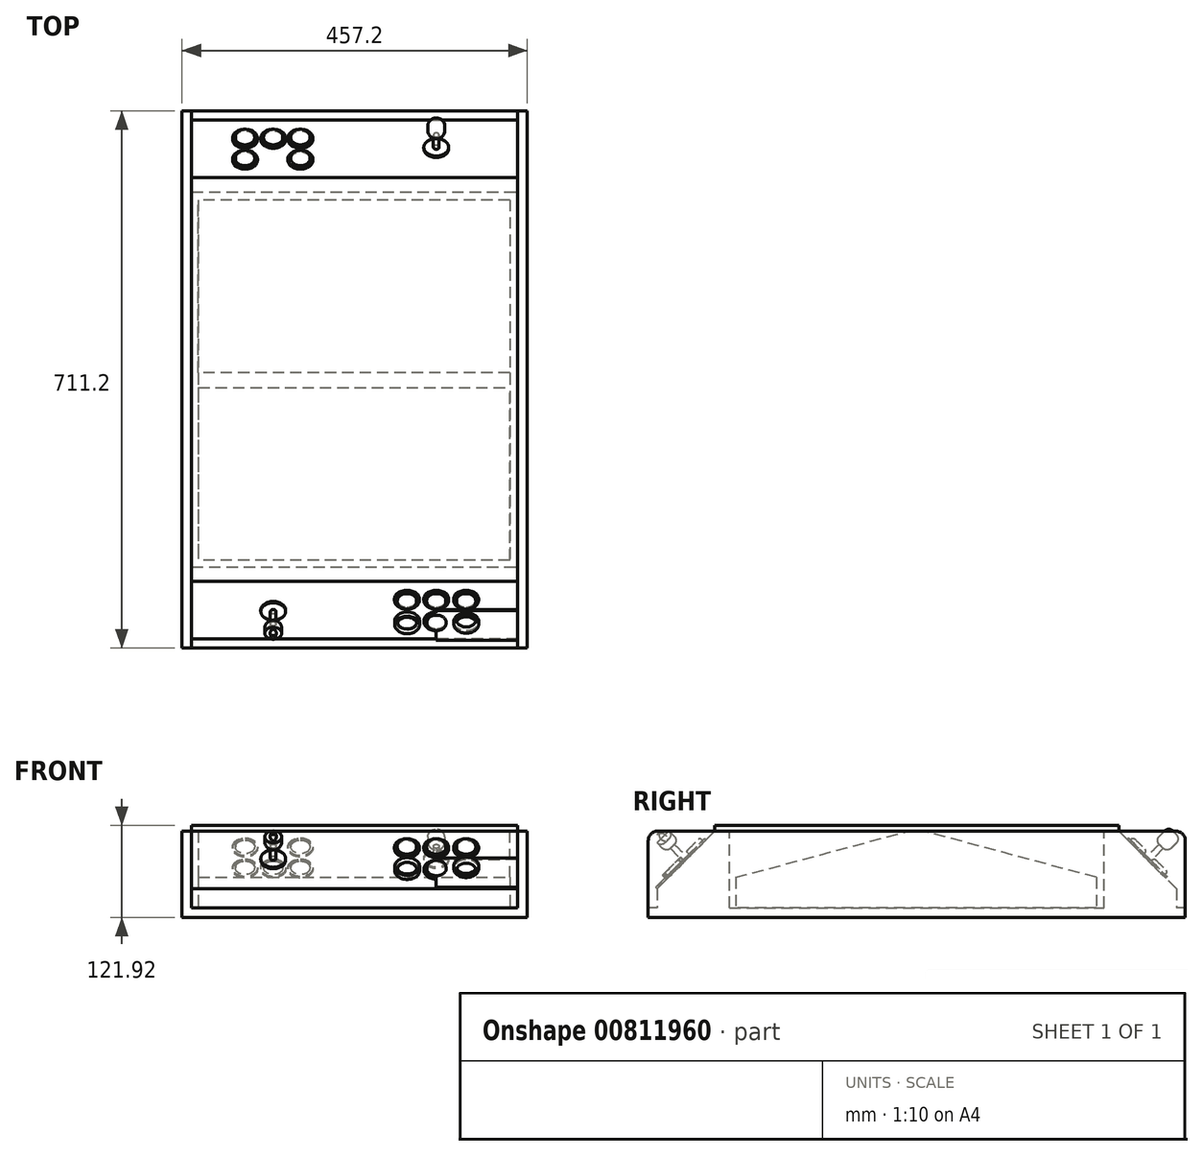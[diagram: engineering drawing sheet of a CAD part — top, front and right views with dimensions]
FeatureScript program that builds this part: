
annotation { "Feature Type Name" : "Feature", "Feature Type Description" : "" }
export const myFeature = defineFeature(function(context is Context, id is Id, definition is map)
    precondition{}
    {
        {
            var Q0;
            Q0=qCreatedBy(makeId("Top.planeOp"),FACE);
            var sketch = newSketch(context, id + "F0", { "sketchPlane" : qUnion([Q0])});
            skLineSegment(sketch, "E0.bottom", {"start": v(-402.64, 582.98) * mm, "end": v(54.56, 582.98) * mm});
            skLineSegment(sketch, "E0.top", {"start": v(-402.64, -128.22) * mm, "end": v(54.56, -128.22) * mm});
            skLineSegment(sketch, "E0.left", {"start": v(-402.64, 582.98) * mm, "end": v(-402.64, -128.22) * mm});
            skLineSegment(sketch, "E0.right", {"start": v(54.56, 582.98) * mm, "end": v(54.56, -128.22) * mm});
            skSolve(sketch);
        }
        {
            var Q0;
            Q0=qSketchRegion(id+"F0",true);
            extrude(context, id + "F1", {"entities" : qUnion([Q0]), "depth" : 12.7 * mm, "offsetDistance" : 25.4 * mm});
        }
        {
            var Q0;
            Q0=makeQuery(id+"F1.opExtrude","CAP_FACE",FACE,{"disambiguationData":[OSD([sQuery(id+"F0.wireOp",EDGE,"E0.bottom"),sQuery(id+"F0.wireOp",EDGE,"E0.top"),sQuery(id+"F0.wireOp",EDGE,"E0.left"),sQuery(id+"F0.wireOp",EDGE,"E0.right")])],"isStart":false});
            var sketch = newSketch(context, id + "F2", { "sketchPlane" : qUnion([Q0])});
            skLineSegment(sketch, "E1.left", {"start": v(54.56, 582.98) * mm, "end": v(54.56, 570.28) * mm});
            skLineSegment(sketch, "E1.right", {"start": v(-402.64, 582.98) * mm, "end": v(-402.64, 570.28) * mm});
            skLineSegment(sketch, "E2.bottom", {"start": v(-402.64, 582.98) * mm, "end": v(-389.94, 582.98) * mm});
            skLineSegment(sketch, "E2.top", {"start": v(-402.64, -128.22) * mm, "end": v(-389.94, -128.22) * mm});
            skLineSegment(sketch, "E2.left", {"start": v(-402.64, 582.98) * mm, "end": v(-402.64, -128.22) * mm});
            skLineSegment(sketch, "E2.right", {"start": v(-389.94, 582.98) * mm, "end": v(-389.94, -128.22) * mm});
            skLineSegment(sketch, "E3.left", {"start": v(54.56, -128.22) * mm, "end": v(54.56, -115.52) * mm});
            skLineSegment(sketch, "E3.right", {"start": v(-402.64, -128.22) * mm, "end": v(-402.64, -115.52) * mm});
            skLineSegment(sketch, "E4.bottom", {"start": v(54.56, 582.98) * mm, "end": v(41.86, 582.98) * mm});
            skLineSegment(sketch, "E4.top", {"start": v(54.56, -128.22) * mm, "end": v(41.86, -128.22) * mm});
            skLineSegment(sketch, "E4.left", {"start": v(54.56, 582.98) * mm, "end": v(54.56, -128.22) * mm});
            skLineSegment(sketch, "E4.right", {"start": v(41.86, 582.98) * mm, "end": v(41.86, -128.22) * mm});
            skSolve(sketch);
        }
        {
            var Q0;
            Q0=qSketchRegion(id+"F2",true);
            extrude(context, id + "F3", {"entities" : qUnion([Q0]), "operationType" : NewBodyOperationType.ADD, "depth" : 101.6 * mm, "offsetDistance" : 25.4 * mm});
        }
        {
            var Q0;
            Q0=makeQuery(id+"F1.opExtrude","CAP_FACE",FACE,{"disambiguationData":[OSD([sQuery(id+"F0.wireOp",EDGE,"E0.bottom"),sQuery(id+"F0.wireOp",EDGE,"E0.top"),sQuery(id+"F0.wireOp",EDGE,"E0.left"),sQuery(id+"F0.wireOp",EDGE,"E0.right")])],"isStart":false});
            var sketch = newSketch(context, id + "F4", { "sketchPlane" : qUnion([Q0])});
            skLineSegment(sketch, "E5.top", {"start": v(41.86, 571.1) * mm, "end": v(-389.94, 571.1) * mm});
            skLineSegment(sketch, "E5.left", {"start": v(41.86, 227.38) * mm, "end": v(41.86, 571.1) * mm});
            skLineSegment(sketch, "E5.right", {"start": v(-389.94, 227.38) * mm, "end": v(-389.94, 571.1) * mm});
            skLineSegment(sketch, "E6.MirrorCS", {"start": v(41.86, -116.33) * mm, "end": v(-389.94, -116.33) * mm});
            skLineSegment(sketch, "E7.MirrorCS", {"start": v(41.86, 227.38) * mm, "end": v(41.86, -116.33) * mm});
            skLineSegment(sketch, "E8.MirrorCS", {"start": v(-389.94, 227.38) * mm, "end": v(-389.94, -116.33) * mm});
            skLineSegment(sketch, "E9", {"start": v(-389.94, 55.53) * mm, "end": v(41.86, 55.53) * mm});
            skLineSegment(sketch, "E10", {"start": v(-389.94, 399.24) * mm, "end": v(41.86, 399.24) * mm});
            skSolve(sketch);
        }
        {
            var Q0;
            Q0=qSketchRegion(id+"F4",true);
            extrude(context, id + "F5", {"entities" : qUnion([Q0]), "operationType" : NewBodyOperationType.ADD, "depth" : 101.6 * mm, "offsetDistance" : 25.4 * mm});
        }
        {
            var Q0;
            Q0=makeQuery(id+"F5.opExtrude","CAP_EDGE",EDGE,{"disambiguationData":[OSD([sQuery(id+"F4.wireOp",EDGE,"E5.top")])],"isStart":false});
            chamfer(context, id + "F6", {"entities" : qUnion([Q0]), "width" : 76.2 * mm, "tangentPropagation" : true});
        }
        {
            var Q0;
            Q0=makeQuery(id+"F3.opExtrude","CAP_EDGE",EDGE,{"disambiguationData":[OSD([sQuery(id+"F2.wireOp",EDGE,"E2.bottom")])],"isStart":false});
            var Q1;
            Q1=makeQuery(id+"F3.opExtrude","CAP_EDGE",EDGE,{"disambiguationData":[OSD([sQuery(id+"F2.wireOp",EDGE,"E4.bottom")])],"isStart":false});
            fillet(context, id + "F7", {"entities" : qUnion([Q0, Q1]), "radius" : 12.7 * mm, "tangentPropagation" : true, "allowEdgeOverflow" : false});
        }
        {
            var Q0;
            Q0=makeQuery(id+"F5.opExtrude","CAP_EDGE",EDGE,{"disambiguationData":[OSD([sQuery(id+"F4.wireOp",EDGE,"E6.MirrorCS")])],"isStart":false});
            chamfer(context, id + "F8", {"entities" : qUnion([Q0]), "width" : 76.2 * mm, "tangentPropagation" : true});
        }
        {
            var Q0;
            Q0=makeQuery(id+"F3.opExtrude","CAP_EDGE",EDGE,{"disambiguationData":[OSD([sQuery(id+"F2.wireOp",EDGE,"E2.top")])],"isStart":false});
            var Q1;
            Q1=makeQuery(id+"F3.opExtrude","CAP_EDGE",EDGE,{"disambiguationData":[OSD([sQuery(id+"F2.wireOp",EDGE,"E4.top")])],"isStart":false});
            fillet(context, id + "F9", {"entities" : qUnion([Q0, Q1]), "radius" : 12.7 * mm, "tangentPropagation" : true, "allowEdgeOverflow" : false});
        }
        {
            var Q0;
            Q0=makeQuery(id+"F5.boolean.opBoolean","MERGE",FACE,{"derivedFrom":[makeQuery(id+"F3.opExtrude","CAP_FACE",FACE,{"disambiguationData":[OSD([sQuery(id+"F2.wireOp",EDGE,"E2.bottom"),sQuery(id+"F2.wireOp",EDGE,"E2.top"),sQuery(id+"F2.wireOp",EDGE,"E2.left"),sQuery(id+"F2.wireOp",EDGE,"E2.right"),sQuery(id+"F2.wireOp",EDGE,"E3.right")])],"isStart":false}),makeQuery(id+"F3.opExtrude","CAP_FACE",FACE,{"disambiguationData":[OSD([sQuery(id+"F2.wireOp",EDGE,"E4.bottom"),sQuery(id+"F2.wireOp",EDGE,"E4.top"),sQuery(id+"F2.wireOp",EDGE,"E4.left"),sQuery(id+"F2.wireOp",EDGE,"E4.right")])],"isStart":false}),makeQuery(id+"F5.opExtrude","CAP_FACE",FACE,{"disambiguationData":[OSD([sQuery(id+"F4.wireOp",EDGE,"E5.top"),sQuery(id+"F4.wireOp",EDGE,"E5.left"),sQuery(id+"F4.wireOp",EDGE,"E5.right"),sQuery(id+"F4.wireOp",EDGE,"E6.MirrorCS"),sQuery(id+"F4.wireOp",EDGE,"E7.MirrorCS"),sQuery(id+"F4.wireOp",EDGE,"E8.MirrorCS")])],"isStart":false})]});
            var sketch = newSketch(context, id + "F10", { "sketchPlane" : qUnion([Q0])});
            skLineSegment(sketch, "E11.bottom", {"start": v(-389.94, -20.7) * mm, "end": v(41.86, -20.7) * mm});
            skLineSegment(sketch, "E11.top", {"start": v(-389.94, 475.34) * mm, "end": v(41.86, 475.34) * mm});
            skLineSegment(sketch, "E11.left", {"start": v(-389.94, -20.7) * mm, "end": v(-389.94, 475.34) * mm});
            skLineSegment(sketch, "E11.right", {"start": v(41.86, -20.7) * mm, "end": v(41.86, 475.34) * mm});
            skSolve(sketch);
        }
        {
            var Q0;
            Q0=makeQuery(id+"F6.opChamfer","BLEND_FACE",FACE,{"disambiguationData":[OSD([sQuery(id+"F4.wireOp",EDGE,"E5.top")])]});
            var sketch = newSketch(context, id + "F11", { "sketchPlane" : qUnion([Q0])});
            skLineSegment(sketch, "E12", {"start": v(174.04, -269.12) * mm, "end": v(174.04, -376.89) * mm});
            skLineSegment(sketch, "E13", {"start": v(174.04, -323) * mm, "end": v(389.94, -323) * mm});
            skLineSegment(sketch, "E14", {"start": v(389.94, -323) * mm, "end": v(-41.86, -323) * mm});
            skLineSegment(sketch, "E15", {"start": v(282, -323) * mm, "end": v(282, -269.12) * mm});
            skLineSegment(sketch, "E16", {"start": v(282, -269.12) * mm, "end": v(282, -376.89) * mm});
            skLineSegment(sketch, "E17", {"start": v(174.04, -376.89) * mm, "end": v(-41.86, -376.89) * mm});
            skLineSegment(sketch, "E18", {"start": v(-41.86, -376.89) * mm, "end": v(66.1, -376.89) * mm});
            skLineSegment(sketch, "E19", {"start": v(66.1, -376.89) * mm, "end": v(66.1, -269.12) * mm});
            skCircle(sketch, "E20", {"center": v(282, -301.12) * mm, "radius": 12.7 * mm});
            skCircle(sketch, "E21", {"center": v(319.4, -301.12) * mm, "radius": 12.7 * mm});
            skCircle(sketch, "E22", {"center": v(245.99, -301.12) * mm, "radius": 12.7 * mm});
            skCircle(sketch, "E23", {"center": v(282, -340.28) * mm, "radius": 12.7 * mm});
            skCircle(sketch, "E24", {"center": v(319.4, -340.28) * mm, "radius": 12.7 * mm});
            skCircle(sketch, "E25", {"center": v(245.99, -340.28) * mm, "radius": 12.7 * mm});
            skCircle(sketch, "E26", {"center": v(245.99, -301.12) * mm, "radius": 16.51 * mm});
            skCircle(sketch, "E27", {"center": v(282, -301.12) * mm, "radius": 16.51 * mm});
            skCircle(sketch, "E28", {"center": v(319.4, -301.12) * mm, "radius": 16.51 * mm});
            skCircle(sketch, "E29", {"center": v(319.4, -340.28) * mm, "radius": 16.51 * mm});
            skCircle(sketch, "E30", {"center": v(282, -340.28) * mm, "radius": 16.51 * mm});
            skCircle(sketch, "E31", {"center": v(245.99, -340.28) * mm, "radius": 16.51 * mm});
            skCircle(sketch, "E32", {"center": v(66.1, -323) * mm, "radius": 16.51 * mm});
            skCircle(sketch, "E33", {"center": v(66.1, -323) * mm, "radius": 3.81 * mm});
            skSolve(sketch);
        }
        {
            var Q0;
            Q0=makeQuery(id+"F11.imprint","IMPRINT",FACE,{"disambiguationData":[TD([[makeQuery(id+"F11.imprint","IMPRINT",EDGE,{"derivedFrom":sQuery(id+"F11.wireOp",EDGE,"E22")}),-1.0]])]});
            var Q1;
            {var subQ0=sQuery(id+"F11.wireOp",EDGE,"E27");var subQ1=sQuery(id+"F11.wireOp",EDGE,"E16");var subQ2=makeQuery(id+"F11.imprint","INTERSECT",VERTEX,{"disambiguationData":[OD(0.0)],"derivedFrom":[subQ1,subQ0]});Q1=makeQuery(id+"F11.imprint","IMPRINT",FACE,{"disambiguationData":[TD([[makeQuery(id+"F11.imprint","IMPRINT",EDGE,{"disambiguationData":[TD([[subQ2,-1.0]])],"derivedFrom":subQ1}),-1.0]])]});}
            var Q2;
            {var subQ0=sQuery(id+"F11.wireOp",EDGE,"E27");var subQ1=sQuery(id+"F11.wireOp",EDGE,"E16");var subQ2=makeQuery(id+"F11.imprint","INTERSECT",VERTEX,{"disambiguationData":[OD(0.0)],"derivedFrom":[subQ1,subQ0]});Q2=makeQuery(id+"F11.imprint","IMPRINT",FACE,{"disambiguationData":[TD([[makeQuery(id+"F11.imprint","IMPRINT",EDGE,{"disambiguationData":[TD([[subQ2,-1.0]])],"derivedFrom":subQ1}),1.0]])]});}
            var Q3;
            Q3=makeQuery(id+"F11.imprint","IMPRINT",FACE,{"disambiguationData":[TD([[makeQuery(id+"F11.imprint","IMPRINT",EDGE,{"derivedFrom":sQuery(id+"F11.wireOp",EDGE,"E21")}),-1.0]])]});
            var Q4;
            Q4=makeQuery(id+"F11.imprint","IMPRINT",FACE,{"disambiguationData":[TD([[makeQuery(id+"F11.imprint","IMPRINT",EDGE,{"derivedFrom":sQuery(id+"F11.wireOp",EDGE,"E24")}),-1.0]])]});
            var Q5;
            {var subQ0=sQuery(id+"F11.wireOp",EDGE,"E30");var subQ1=sQuery(id+"F11.wireOp",EDGE,"E16");var subQ2=makeQuery(id+"F11.imprint","INTERSECT",VERTEX,{"disambiguationData":[OD(0.0)],"derivedFrom":[subQ1,subQ0]});Q5=makeQuery(id+"F11.imprint","IMPRINT",FACE,{"disambiguationData":[TD([[makeQuery(id+"F11.imprint","IMPRINT",EDGE,{"disambiguationData":[TD([[subQ2,-1.0]])],"derivedFrom":subQ1}),1.0]])]});}
            var Q6;
            {var subQ0=sQuery(id+"F11.wireOp",EDGE,"E30");var subQ1=sQuery(id+"F11.wireOp",EDGE,"E16");var subQ2=makeQuery(id+"F11.imprint","INTERSECT",VERTEX,{"disambiguationData":[OD(0.0)],"derivedFrom":[subQ1,subQ0]});Q6=makeQuery(id+"F11.imprint","IMPRINT",FACE,{"disambiguationData":[TD([[makeQuery(id+"F11.imprint","IMPRINT",EDGE,{"disambiguationData":[TD([[subQ2,-1.0]])],"derivedFrom":subQ1}),-1.0]])]});}
            var Q7;
            Q7=makeQuery(id+"F11.imprint","IMPRINT",FACE,{"disambiguationData":[TD([[makeQuery(id+"F11.imprint","IMPRINT",EDGE,{"derivedFrom":sQuery(id+"F11.wireOp",EDGE,"E25")}),-1.0]])]});
            extrude(context, id + "F12", {"entities" : qUnion([Q0, Q1, Q2, Q3, Q4, Q5, Q6, Q7]), "operationType" : NewBodyOperationType.ADD, "depth" : 2.54 * mm, "offsetDistance" : 25.4 * mm});
        }
        {
            var Q0;
            Q0=makeQuery(id+"F11.imprint","IMPRINT",FACE,{"disambiguationData":[TD([[makeQuery(id+"F11.imprint","IMPRINT",EDGE,{"derivedFrom":sQuery(id+"F11.wireOp",EDGE,"E22")}),1.0]])]});
            var Q1;
            {var subQ0=sQuery(id+"F11.wireOp",EDGE,"E20");var subQ1=sQuery(id+"F11.wireOp",EDGE,"E16");var subQ2=makeQuery(id+"F11.imprint","INTERSECT",VERTEX,{"disambiguationData":[OD(0.0)],"derivedFrom":[subQ1,subQ0]});Q1=makeQuery(id+"F11.imprint","IMPRINT",FACE,{"disambiguationData":[TD([[makeQuery(id+"F11.imprint","IMPRINT",EDGE,{"disambiguationData":[TD([[subQ2,-1.0]])],"derivedFrom":subQ1}),-1.0]])]});}
            var Q2;
            {var subQ0=sQuery(id+"F11.wireOp",EDGE,"E20");var subQ1=sQuery(id+"F11.wireOp",EDGE,"E16");var subQ2=makeQuery(id+"F11.imprint","INTERSECT",VERTEX,{"disambiguationData":[OD(0.0)],"derivedFrom":[subQ1,subQ0]});Q2=makeQuery(id+"F11.imprint","IMPRINT",FACE,{"disambiguationData":[TD([[makeQuery(id+"F11.imprint","IMPRINT",EDGE,{"disambiguationData":[TD([[subQ2,-1.0]])],"derivedFrom":subQ1}),1.0]])]});}
            var Q3;
            Q3=makeQuery(id+"F11.imprint","IMPRINT",FACE,{"disambiguationData":[TD([[makeQuery(id+"F11.imprint","IMPRINT",EDGE,{"derivedFrom":sQuery(id+"F11.wireOp",EDGE,"E21")}),1.0]])]});
            var Q4;
            Q4=makeQuery(id+"F11.imprint","IMPRINT",FACE,{"disambiguationData":[TD([[makeQuery(id+"F11.imprint","IMPRINT",EDGE,{"derivedFrom":sQuery(id+"F11.wireOp",EDGE,"E24")}),1.0]])]});
            var Q5;
            {var subQ0=sQuery(id+"F11.wireOp",EDGE,"E23");var subQ1=sQuery(id+"F11.wireOp",EDGE,"E16");var subQ2=makeQuery(id+"F11.imprint","INTERSECT",VERTEX,{"disambiguationData":[OD(0.0)],"derivedFrom":[subQ1,subQ0]});Q5=makeQuery(id+"F11.imprint","IMPRINT",FACE,{"disambiguationData":[TD([[makeQuery(id+"F11.imprint","IMPRINT",EDGE,{"disambiguationData":[TD([[subQ2,-1.0]])],"derivedFrom":subQ1}),1.0]])]});}
            var Q6;
            {var subQ0=sQuery(id+"F11.wireOp",EDGE,"E23");var subQ1=sQuery(id+"F11.wireOp",EDGE,"E16");var subQ2=makeQuery(id+"F11.imprint","INTERSECT",VERTEX,{"disambiguationData":[OD(0.0)],"derivedFrom":[subQ1,subQ0]});Q6=makeQuery(id+"F11.imprint","IMPRINT",FACE,{"disambiguationData":[TD([[makeQuery(id+"F11.imprint","IMPRINT",EDGE,{"disambiguationData":[TD([[subQ2,-1.0]])],"derivedFrom":subQ1}),-1.0]])]});}
            var Q7;
            Q7=makeQuery(id+"F11.imprint","IMPRINT",FACE,{"disambiguationData":[TD([[makeQuery(id+"F11.imprint","IMPRINT",EDGE,{"derivedFrom":sQuery(id+"F11.wireOp",EDGE,"E25")}),1.0]])]});
            extrude(context, id + "F13", {"entities" : qUnion([Q0, Q1, Q2, Q3, Q4, Q5, Q6, Q7]), "operationType" : NewBodyOperationType.ADD, "depth" : 7.62 * mm, "offsetDistance" : 25.4 * mm});
        }
        {
            var Q0;
            Q0=makeQuery(id+"F13.opExtrude","CAP_EDGE",EDGE,{"disambiguationData":[OSD([sQuery(id+"F11.wireOp",EDGE,"E23")])],"isStart":false});
            var Q1;
            Q1=makeQuery(id+"F13.opExtrude","CAP_EDGE",EDGE,{"disambiguationData":[OSD([sQuery(id+"F11.wireOp",EDGE,"E24")])],"isStart":false});
            var Q2;
            Q2=makeQuery(id+"F13.opExtrude","CAP_EDGE",EDGE,{"disambiguationData":[OSD([sQuery(id+"F11.wireOp",EDGE,"E21")])],"isStart":false});
            var Q3;
            Q3=makeQuery(id+"F13.opExtrude","CAP_EDGE",EDGE,{"disambiguationData":[OSD([sQuery(id+"F11.wireOp",EDGE,"E20")])],"isStart":false});
            var Q4;
            Q4=makeQuery(id+"F13.opExtrude","CAP_EDGE",EDGE,{"disambiguationData":[OSD([sQuery(id+"F11.wireOp",EDGE,"E22")])],"isStart":false});
            var Q5;
            Q5=makeQuery(id+"F13.opExtrude","CAP_EDGE",EDGE,{"disambiguationData":[OSD([sQuery(id+"F11.wireOp",EDGE,"E25")])],"isStart":false});
            fillet(context, id + "F14", {"entities" : qUnion([Q0, Q1, Q2, Q3, Q4, Q5]), "radius" : 2.54 * mm, "tangentPropagation" : true, "allowEdgeOverflow" : false});
        }
        {
            var Q0;
            {var subQ0=sQuery(id+"F11.wireOp",EDGE,"E32");var subQ1=sQuery(id+"F11.wireOp",EDGE,"E14");var subQ2=makeQuery(id+"F11.imprint","INTERSECT",VERTEX,{"disambiguationData":[OD(0.0)],"derivedFrom":[subQ1,subQ0]});Q0=makeQuery(id+"F11.imprint","IMPRINT",FACE,{"disambiguationData":[TD([[makeQuery(id+"F11.imprint","IMPRINT",EDGE,{"disambiguationData":[TD([[subQ2,-1.0]])],"derivedFrom":subQ1}),-1.0]])]});}
            var Q1;
            {var subQ0=sQuery(id+"F11.wireOp",EDGE,"E33");var subQ1=sQuery(id+"F11.wireOp",EDGE,"E14");var subQ2=makeQuery(id+"F11.imprint","INTERSECT",VERTEX,{"disambiguationData":[OD(1.0)],"derivedFrom":[subQ1,subQ0]});Q1=makeQuery(id+"F11.imprint","IMPRINT",FACE,{"disambiguationData":[TD([[makeQuery(id+"F11.imprint","IMPRINT",EDGE,{"disambiguationData":[TD([[subQ2,-1.0]])],"derivedFrom":subQ1}),-1.0]])]});}
            var Q2;
            {var subQ0=sQuery(id+"F11.wireOp",EDGE,"E33");var subQ1=sQuery(id+"F11.wireOp",EDGE,"E14");var subQ2=makeQuery(id+"F11.imprint","INTERSECT",VERTEX,{"disambiguationData":[OD(1.0)],"derivedFrom":[subQ1,subQ0]});Q2=makeQuery(id+"F11.imprint","IMPRINT",FACE,{"disambiguationData":[TD([[makeQuery(id+"F11.imprint","IMPRINT",EDGE,{"disambiguationData":[TD([[subQ2,-1.0]])],"derivedFrom":subQ1}),1.0]])]});}
            var Q3;
            {var subQ0=sQuery(id+"F11.wireOp",EDGE,"E32");var subQ1=sQuery(id+"F11.wireOp",EDGE,"E14");var subQ2=makeQuery(id+"F11.imprint","INTERSECT",VERTEX,{"disambiguationData":[OD(0.0)],"derivedFrom":[subQ1,subQ0]});Q3=makeQuery(id+"F11.imprint","IMPRINT",FACE,{"disambiguationData":[TD([[makeQuery(id+"F11.imprint","IMPRINT",EDGE,{"disambiguationData":[TD([[subQ2,-1.0]])],"derivedFrom":subQ1}),1.0]])]});}
            extrude(context, id + "F15", {"entities" : qUnion([Q0, Q1, Q2, Q3]), "operationType" : NewBodyOperationType.ADD, "depth" : 2.54 * mm, "offsetDistance" : 25.4 * mm});
        }
        {
            var Q0;
            {var subQ0=sQuery(id+"F11.wireOp",EDGE,"E33");var subQ1=sQuery(id+"F11.wireOp",EDGE,"E14");var subQ2=makeQuery(id+"F11.imprint","INTERSECT",VERTEX,{"disambiguationData":[OD(0.0)],"derivedFrom":[subQ1,subQ0]});Q0=makeQuery(id+"F11.imprint","IMPRINT",FACE,{"disambiguationData":[TD([[makeQuery(id+"F11.imprint","IMPRINT",EDGE,{"disambiguationData":[TD([[subQ2,-1.0]])],"derivedFrom":subQ1}),1.0]])]});}
            var Q1;
            {var subQ0=sQuery(id+"F11.wireOp",EDGE,"E33");var subQ1=sQuery(id+"F11.wireOp",EDGE,"E14");var subQ2=makeQuery(id+"F11.imprint","INTERSECT",VERTEX,{"disambiguationData":[OD(0.0)],"derivedFrom":[subQ1,subQ0]});Q1=makeQuery(id+"F11.imprint","IMPRINT",FACE,{"disambiguationData":[TD([[makeQuery(id+"F11.imprint","IMPRINT",EDGE,{"disambiguationData":[TD([[subQ2,-1.0]])],"derivedFrom":subQ1}),-1.0]])]});}
            var Q2;
            {var subQ0=sQuery(id+"F11.wireOp",EDGE,"E19");var subQ1=sQuery(id+"F11.wireOp",EDGE,"E14");var subQ2=makeQuery(id+"F11.imprint","INTERSECT",VERTEX,{"derivedFrom":[subQ1,subQ0]});Q2=makeQuery(id+"F11.imprint","IMPRINT",FACE,{"disambiguationData":[TD([[makeQuery(id+"F11.imprint","IMPRINT",EDGE,{"disambiguationData":[TD([[subQ2,-1.0]])],"derivedFrom":subQ1}),-1.0]])]});}
            var Q3;
            {var subQ0=sQuery(id+"F11.wireOp",EDGE,"E19");var subQ1=sQuery(id+"F11.wireOp",EDGE,"E14");var subQ2=makeQuery(id+"F11.imprint","INTERSECT",VERTEX,{"derivedFrom":[subQ1,subQ0]});Q3=makeQuery(id+"F11.imprint","IMPRINT",FACE,{"disambiguationData":[TD([[makeQuery(id+"F11.imprint","IMPRINT",EDGE,{"disambiguationData":[TD([[subQ2,-1.0]])],"derivedFrom":subQ1}),1.0]])]});}
            extrude(context, id + "F16", {"entities" : qUnion([Q0, Q1, Q2, Q3]), "operationType" : NewBodyOperationType.ADD, "depth" : 25.4 * mm, "offsetDistance" : 25.4 * mm});
        }
        {
            var Q0;
            Q0=makeQuery(id+"F16.opExtrude","CAP_FACE",FACE,{"disambiguationData":[OSD([sQuery(id+"F11.wireOp",EDGE,"E33")])],"isStart":false});
            var sketch = newSketch(context, id + "F17", { "sketchPlane" : qUnion([Q0])});
            skCircle(sketch, "E34", {"center": v(66.1, -323) * mm, "radius": 11.12 * mm});
            skSolve(sketch);
        }
        {
            var Q0;
            Q0=qSketchRegion(id+"F17",true);
            extrude(context, id + "F18", {"entities" : qUnion([Q0]), "operationType" : NewBodyOperationType.ADD, "depth" : 25.4 * mm, "offsetDistance" : 25.4 * mm});
        }
        {
            var Q0;
            Q0=makeQuery(id+"F18.opExtrude","CAP_EDGE",EDGE,{"disambiguationData":[OSD([sQuery(id+"F17.wireOp",EDGE,"E34")])],"isStart":false});
            var Q1;
            Q1=makeQuery(id+"F18.opExtrude","CAP_EDGE",EDGE,{"disambiguationData":[OSD([sQuery(id+"F17.wireOp",EDGE,"E34")])],"isStart":true});
            fillet(context, id + "F19", {"entities" : qUnion([Q0, Q1]), "radius" : 7.62 * mm, "tangentPropagation" : true, "allowEdgeOverflow" : false});
        }
        {
            var Q0;
            Q0=makeQuery(id+"F8.opChamfer","BLEND_FACE",FACE,{"disambiguationData":[OSD([sQuery(id+"F4.wireOp",EDGE,"E6.MirrorCS")])]});
            var sketch = newSketch(context, id + "F20", { "sketchPlane" : qUnion([Q0])});
            skLineSegment(sketch, "E35", {"start": v(-174.04, 52.44) * mm, "end": v(-174.04, -55.32) * mm});
            skLineSegment(sketch, "E36", {"start": v(-389.94, 52.44) * mm, "end": v(41.86, 52.44) * mm});
            skLineSegment(sketch, "E37", {"start": v(-174.04, -1.44) * mm, "end": v(-66.1, -1.44) * mm});
            skPoint(sketch, "E37.endSnap0", {"position": v(-174.04, -1.44) * mm});
            skLineSegment(sketch, "E38", {"start": v(-174.04, -1.44) * mm, "end": v(-282, -1.44) * mm});
            skLineSegment(sketch, "E39", {"start": v(-66.1, 52.44) * mm, "end": v(-66.1, -55.32) * mm});
            skLineSegment(sketch, "E40", {"start": v(-282, 52.44) * mm, "end": v(-282, -55.32) * mm});
            skCircle(sketch, "E41", {"center": v(-66.1, 19.45) * mm, "radius": 16.51 * mm});
            skCircle(sketch, "E42", {"center": v(-26.68, 19.45) * mm, "radius": 16.51 * mm});
            skCircle(sketch, "E43", {"center": v(-104.94, 19.45) * mm, "radius": 16.51 * mm});
            skCircle(sketch, "E44", {"center": v(-26.68, 19.45) * mm, "radius": 12.7 * mm});
            skCircle(sketch, "E45", {"center": v(-66.1, 19.45) * mm, "radius": 12.7 * mm});
            skCircle(sketch, "E46", {"center": v(-104.94, 19.45) * mm, "radius": 12.7 * mm});
            skLineSegment(sketch, "E47", {"start": v(-174.04, -1.44) * mm, "end": v(41.86, 0) * mm});
            skCircle(sketch, "E48.MirrorC", {"center": v(-104.67, -21.4) * mm, "radius": 12.7 * mm});
            skCircle(sketch, "E49.MirrorC", {"center": v(-26.41, -20.36) * mm, "radius": 16.51 * mm});
            skCircle(sketch, "E50.MirrorC", {"center": v(-104.67, -21.4) * mm, "radius": 16.51 * mm});
            skCircle(sketch, "E51.MirrorC", {"center": v(-65.82, -20.88) * mm, "radius": 16.51 * mm});
            skCircle(sketch, "E52.MirrorC", {"center": v(-65.82, -20.88) * mm, "radius": 12.7 * mm});
            skCircle(sketch, "E53.MirrorC", {"center": v(-26.41, -20.36) * mm, "radius": 12.7 * mm});
            skCircle(sketch, "E54", {"center": v(-282, -1.44) * mm, "radius": 16.51 * mm});
            skCircle(sketch, "E55", {"center": v(-282, -1.44) * mm, "radius": 3.81 * mm});
            skSolve(sketch);
        }
        {
            var Q0;
            Q0=makeQuery(id+"F20.imprint","IMPRINT",FACE,{"disambiguationData":[TD([[makeQuery(id+"F20.imprint","IMPRINT",EDGE,{"derivedFrom":sQuery(id+"F20.wireOp",EDGE,"E43")}),1.0]])]});
            var Q1;
            {var subQ0=sQuery(id+"F20.wireOp",EDGE,"E41");var subQ1=sQuery(id+"F20.wireOp",EDGE,"E39");var subQ2=makeQuery(id+"F20.imprint","INTERSECT",VERTEX,{"disambiguationData":[OD(0.0)],"derivedFrom":[subQ1,subQ0]});Q1=makeQuery(id+"F20.imprint","IMPRINT",FACE,{"disambiguationData":[TD([[makeQuery(id+"F20.imprint","IMPRINT",EDGE,{"disambiguationData":[TD([[subQ2,-1.0]])],"derivedFrom":subQ1}),-1.0]])]});}
            var Q2;
            {var subQ0=sQuery(id+"F20.wireOp",EDGE,"E41");var subQ1=sQuery(id+"F20.wireOp",EDGE,"E39");var subQ2=makeQuery(id+"F20.imprint","INTERSECT",VERTEX,{"disambiguationData":[OD(0.0)],"derivedFrom":[subQ1,subQ0]});Q2=makeQuery(id+"F20.imprint","IMPRINT",FACE,{"disambiguationData":[TD([[makeQuery(id+"F20.imprint","IMPRINT",EDGE,{"disambiguationData":[TD([[subQ2,-1.0]])],"derivedFrom":subQ1}),1.0]])]});}
            var Q3;
            Q3=makeQuery(id+"F20.imprint","IMPRINT",FACE,{"disambiguationData":[TD([[makeQuery(id+"F20.imprint","IMPRINT",EDGE,{"derivedFrom":sQuery(id+"F20.wireOp",EDGE,"E42")}),1.0]])]});
            var Q4;
            Q4=makeQuery(id+"F20.imprint","IMPRINT",FACE,{"disambiguationData":[TD([[makeQuery(id+"F20.imprint","IMPRINT",EDGE,{"derivedFrom":sQuery(id+"F20.wireOp",EDGE,"E49.MirrorC")}),-1.0]])]});
            var Q5;
            {var subQ0=sQuery(id+"F20.wireOp",EDGE,"E51.MirrorC");var subQ1=sQuery(id+"F20.wireOp",EDGE,"E39");var subQ2=makeQuery(id+"F20.imprint","INTERSECT",VERTEX,{"disambiguationData":[OD(0.0)],"derivedFrom":[subQ1,subQ0]});Q5=makeQuery(id+"F20.imprint","IMPRINT",FACE,{"disambiguationData":[TD([[makeQuery(id+"F20.imprint","IMPRINT",EDGE,{"disambiguationData":[TD([[subQ2,-1.0]])],"derivedFrom":subQ1}),1.0]])]});}
            var Q6;
            {var subQ0=sQuery(id+"F20.wireOp",EDGE,"E51.MirrorC");var subQ1=sQuery(id+"F20.wireOp",EDGE,"E39");var subQ2=makeQuery(id+"F20.imprint","INTERSECT",VERTEX,{"disambiguationData":[OD(0.0)],"derivedFrom":[subQ1,subQ0]});Q6=makeQuery(id+"F20.imprint","IMPRINT",FACE,{"disambiguationData":[TD([[makeQuery(id+"F20.imprint","IMPRINT",EDGE,{"disambiguationData":[TD([[subQ2,-1.0]])],"derivedFrom":subQ1}),-1.0]])]});}
            var Q7;
            Q7=makeQuery(id+"F20.imprint","IMPRINT",FACE,{"disambiguationData":[TD([[makeQuery(id+"F20.imprint","IMPRINT",EDGE,{"derivedFrom":sQuery(id+"F20.wireOp",EDGE,"E48.MirrorC")}),1.0]])]});
            extrude(context, id + "F21", {"entities" : qUnion([Q0, Q1, Q2, Q3, Q4, Q5, Q6, Q7]), "operationType" : NewBodyOperationType.ADD, "depth" : 2.54 * mm, "offsetDistance" : 25.4 * mm});
        }
        {
            var Q0;
            Q0=makeQuery(id+"F20.imprint","IMPRINT",FACE,{"disambiguationData":[TD([[makeQuery(id+"F20.imprint","IMPRINT",EDGE,{"derivedFrom":sQuery(id+"F20.wireOp",EDGE,"E46")}),1.0]])]});
            var Q1;
            {var subQ0=sQuery(id+"F20.wireOp",EDGE,"E45");var subQ1=sQuery(id+"F20.wireOp",EDGE,"E39");var subQ2=makeQuery(id+"F20.imprint","INTERSECT",VERTEX,{"disambiguationData":[OD(0.0)],"derivedFrom":[subQ1,subQ0]});Q1=makeQuery(id+"F20.imprint","IMPRINT",FACE,{"disambiguationData":[TD([[makeQuery(id+"F20.imprint","IMPRINT",EDGE,{"disambiguationData":[TD([[subQ2,-1.0]])],"derivedFrom":subQ1}),-1.0]])]});}
            var Q2;
            {var subQ0=sQuery(id+"F20.wireOp",EDGE,"E45");var subQ1=sQuery(id+"F20.wireOp",EDGE,"E39");var subQ2=makeQuery(id+"F20.imprint","INTERSECT",VERTEX,{"disambiguationData":[OD(0.0)],"derivedFrom":[subQ1,subQ0]});Q2=makeQuery(id+"F20.imprint","IMPRINT",FACE,{"disambiguationData":[TD([[makeQuery(id+"F20.imprint","IMPRINT",EDGE,{"disambiguationData":[TD([[subQ2,-1.0]])],"derivedFrom":subQ1}),1.0]])]});}
            var Q3;
            Q3=makeQuery(id+"F20.imprint","IMPRINT",FACE,{"disambiguationData":[TD([[makeQuery(id+"F20.imprint","IMPRINT",EDGE,{"derivedFrom":sQuery(id+"F20.wireOp",EDGE,"E44")}),1.0]])]});
            var Q4;
            Q4=makeQuery(id+"F20.imprint","IMPRINT",FACE,{"disambiguationData":[TD([[makeQuery(id+"F20.imprint","IMPRINT",EDGE,{"derivedFrom":sQuery(id+"F20.wireOp",EDGE,"E53.MirrorC")}),-1.0]])]});
            var Q5;
            {var subQ0=sQuery(id+"F20.wireOp",EDGE,"E52.MirrorC");var subQ1=sQuery(id+"F20.wireOp",EDGE,"E39");var subQ2=makeQuery(id+"F20.imprint","INTERSECT",VERTEX,{"disambiguationData":[OD(0.0)],"derivedFrom":[subQ1,subQ0]});Q5=makeQuery(id+"F20.imprint","IMPRINT",FACE,{"disambiguationData":[TD([[makeQuery(id+"F20.imprint","IMPRINT",EDGE,{"disambiguationData":[TD([[subQ2,-1.0]])],"derivedFrom":subQ1}),1.0]])]});}
            var Q6;
            {var subQ0=sQuery(id+"F20.wireOp",EDGE,"E52.MirrorC");var subQ1=sQuery(id+"F20.wireOp",EDGE,"E39");var subQ2=makeQuery(id+"F20.imprint","INTERSECT",VERTEX,{"disambiguationData":[OD(0.0)],"derivedFrom":[subQ1,subQ0]});Q6=makeQuery(id+"F20.imprint","IMPRINT",FACE,{"disambiguationData":[TD([[makeQuery(id+"F20.imprint","IMPRINT",EDGE,{"disambiguationData":[TD([[subQ2,-1.0]])],"derivedFrom":subQ1}),-1.0]])]});}
            var Q7;
            Q7=makeQuery(id+"F20.imprint","IMPRINT",FACE,{"disambiguationData":[TD([[makeQuery(id+"F20.imprint","IMPRINT",EDGE,{"derivedFrom":sQuery(id+"F20.wireOp",EDGE,"E48.MirrorC")}),-1.0]])]});
            extrude(context, id + "F22", {"entities" : qUnion([Q0, Q1, Q2, Q3, Q4, Q5, Q6, Q7]), "operationType" : NewBodyOperationType.ADD, "depth" : 7.62 * mm, "offsetDistance" : 25.4 * mm});
        }
        {
            var Q0;
            Q0=makeQuery(id+"F22.opExtrude","CAP_EDGE",EDGE,{"disambiguationData":[OSD([sQuery(id+"F20.wireOp",EDGE,"E46")])],"isStart":false});
            var Q1;
            Q1=makeQuery(id+"F22.opExtrude","CAP_EDGE",EDGE,{"disambiguationData":[OSD([sQuery(id+"F20.wireOp",EDGE,"E45")])],"isStart":false});
            var Q2;
            Q2=makeQuery(id+"F22.opExtrude","CAP_EDGE",EDGE,{"disambiguationData":[OSD([sQuery(id+"F20.wireOp",EDGE,"E44")])],"isStart":false});
            var Q3;
            Q3=makeQuery(id+"F22.opExtrude","CAP_EDGE",EDGE,{"disambiguationData":[OSD([sQuery(id+"F20.wireOp",EDGE,"E52.MirrorC")])],"isStart":false});
            var Q4;
            Q4=makeQuery(id+"F22.opExtrude","CAP_EDGE",EDGE,{"disambiguationData":[OSD([sQuery(id+"F20.wireOp",EDGE,"E53.MirrorC")])],"isStart":false});
            var Q5;
            Q5=makeQuery(id+"F22.opExtrude","CAP_EDGE",EDGE,{"disambiguationData":[OSD([sQuery(id+"F20.wireOp",EDGE,"E48.MirrorC")])],"isStart":false});
            fillet(context, id + "F23", {"entities" : qUnion([Q0, Q1, Q2, Q3, Q4, Q5]), "radius" : 2.54 * mm, "tangentPropagation" : true, "allowEdgeOverflow" : false});
        }
        {
            var Q0;
            {var subQ0=sQuery(id+"F20.wireOp",EDGE,"E54");var subQ1=sQuery(id+"F20.wireOp",EDGE,"E38");var subQ2=makeQuery(id+"F20.imprint","INTERSECT",VERTEX,{"derivedFrom":[subQ1,subQ0]});Q0=makeQuery(id+"F20.imprint","IMPRINT",FACE,{"disambiguationData":[TD([[makeQuery(id+"F20.imprint","IMPRINT",EDGE,{"disambiguationData":[TD([[subQ2,-1.0]])],"derivedFrom":subQ1}),-1.0]])]});}
            var Q1;
            {var subQ0=sQuery(id+"F20.wireOp",EDGE,"E54");var subQ1=sQuery(id+"F20.wireOp",EDGE,"E38");var subQ2=makeQuery(id+"F20.imprint","INTERSECT",VERTEX,{"derivedFrom":[subQ1,subQ0]});Q1=makeQuery(id+"F20.imprint","IMPRINT",FACE,{"disambiguationData":[TD([[makeQuery(id+"F20.imprint","IMPRINT",EDGE,{"disambiguationData":[TD([[subQ2,-1.0]])],"derivedFrom":subQ1}),1.0]])]});}
            var Q2;
            {var subQ0=sQuery(id+"F20.wireOp",EDGE,"E54");var subQ1=sQuery(id+"F20.wireOp",EDGE,"E40");var subQ2=makeQuery(id+"F20.imprint","INTERSECT",VERTEX,{"disambiguationData":[OD(0.0)],"derivedFrom":[subQ1,subQ0]});Q2=makeQuery(id+"F20.imprint","IMPRINT",FACE,{"disambiguationData":[TD([[makeQuery(id+"F20.imprint","IMPRINT",EDGE,{"disambiguationData":[TD([[subQ2,-1.0]])],"derivedFrom":subQ1}),-1.0]])]});}
            extrude(context, id + "F24", {"entities" : qUnion([Q0, Q1, Q2]), "operationType" : NewBodyOperationType.ADD, "depth" : 2.54 * mm, "offsetDistance" : 25.4 * mm});
        }
        {
            var Q0;
            {var subQ0=sQuery(id+"F4.wireOp",EDGE,"E6.MirrorCS");var subQ1=sQuery(id+"F2.wireOp",EDGE,"E2.right");Q0=makeQuery(id+"F24.boolean.opBoolean","SPLIT",FACE,{"disambiguationData":[TD([makeQuery(id+"F24.opExtrude","SWEPT_FACE",FACE,{"disambiguationData":[OSD([sQuery(id+"F20.wireOp",EDGE,"E55")])]})])],"derivedFrom":makeQuery(id+"F21.boolean.opBoolean","SPLIT",FACE,{"disambiguationData":[TD([makeQuery(id+"F3.opExtrude","SWEPT_FACE",FACE,{"disambiguationData":[OSD([subQ1])]})])],"derivedFrom":makeQuery(id+"F8.opChamfer","BLEND_FACE",FACE,{"disambiguationData":[OSD([subQ0])]})})});}
            extrude(context, id + "F25", {"entities" : qUnion([Q0]), "operationType" : NewBodyOperationType.ADD, "depth" : 25.4 * mm, "offsetDistance" : 25.4 * mm});
        }
        {
            var Q0;
            Q0=makeQuery(id+"F25.opExtrude","CAP_FACE",FACE,{"disambiguationData":[OSD([sQuery(id+"F4.wireOp",EDGE,"E6.MirrorCS")])],"isStart":false});
            var sketch = newSketch(context, id + "F26", { "sketchPlane" : qUnion([Q0])});
            skCircle(sketch, "E56", {"center": v(-282, -1.44) * mm, "radius": 11.12 * mm});
            skSolve(sketch);
        }
        {
            var Q0;
            Q0=qSketchRegion(id+"F26",true);
            extrude(context, id + "F27", {"entities" : qUnion([Q0]), "operationType" : NewBodyOperationType.ADD, "depth" : 25.4 * mm, "offsetDistance" : 25.4 * mm});
        }
        {
            var Q0;
            Q0=makeQuery(id+"F27.opExtrude","CAP_EDGE",EDGE,{"disambiguationData":[OSD([sQuery(id+"F26.wireOp",EDGE,"E56")])],"isStart":false});
            var Q1;
            Q1=makeQuery(id+"F27.opExtrude","CAP_EDGE",EDGE,{"disambiguationData":[OSD([sQuery(id+"F26.wireOp",EDGE,"E56")])],"isStart":true});
            fillet(context, id + "F28", {"entities" : qUnion([Q0, Q1]), "radius" : 7.62 * mm, "tangentPropagation" : true, "allowEdgeOverflow" : false});
        }
        {
            var Q0;
            Q0=makeQuery(id+"F10.imprint","IMPRINT",FACE,{"disambiguationData":[TD([[makeQuery(id+"F10.imprint","IMPRINT",EDGE,{"derivedFrom":sQuery(id+"F10.wireOp",EDGE,"E11.bottom")}),1.0]])]});
            extrude(context, id + "F29", {"entities" : qUnion([Q0]), "operationType" : NewBodyOperationType.REMOVE, "oppositeDirection" : true, "depth" : 101.6 * mm, "offsetDistance" : 25.4 * mm});
        }
        {
            var Q0;
            Q0=makeQuery(id+"F29.boolean.opBoolean","COPY",FACE,{"derivedFrom":makeQuery(id+"F29.opExtrude","CAP_FACE",FACE,{"disambiguationData":[OSD([sQuery(id+"F10.wireOp",EDGE,"E11.bottom"),sQuery(id+"F10.wireOp",EDGE,"E11.top"),sQuery(id+"F10.wireOp",EDGE,"E11.left"),sQuery(id+"F10.wireOp",EDGE,"E11.right")])],"isStart":false})});
            var sketch = newSketch(context, id + "F30", { "sketchPlane" : qUnion([Q0])});
            skLineSegment(sketch, "E57.bottom", {"start": v(31.4, 465.04) * mm, "end": v(-381.22, 465.04) * mm});
            skLineSegment(sketch, "E57.top", {"start": v(31.4, -12.26) * mm, "end": v(-381.22, -12.26) * mm});
            skLineSegment(sketch, "E57.left", {"start": v(31.4, 465.04) * mm, "end": v(31.4, -12.26) * mm});
            skLineSegment(sketch, "E57.right", {"start": v(-381.22, 465.04) * mm, "end": v(-381.22, -12.26) * mm});
            skSolve(sketch);
        }
        {
            var Q0;
            Q0=qSketchRegion(id+"F30",true);
            extrude(context, id + "F31", {"entities" : qUnion([Q0]), "operationType" : NewBodyOperationType.ADD, "depth" : 101.6 * mm, "offsetDistance" : 25.4 * mm});
        }
        {
            var Q0;
            Q0=makeQuery(id+"F31.opExtrude","CAP_EDGE",EDGE,{"disambiguationData":[OSD([sQuery(id+"F30.wireOp",EDGE,"E57.bottom")])],"isStart":false});
            var Q1;
            Q1=makeQuery(id+"F31.opExtrude","CAP_EDGE",EDGE,{"disambiguationData":[OSD([sQuery(id+"F30.wireOp",EDGE,"E57.top")])],"isStart":false});
            chamfer(context, id + "F32", {"entities" : qUnion([Q0, Q1]), "chamferType" : ChamferType.OFFSET_ANGLE, "width" : 228.6 * mm, "oppositeDirection" : false, "angle" : 15 * degree, "tangentPropagation" : true});
        }
        {
            var Q0;
            Q0=makeQuery(id+"F5.boolean.opBoolean","MERGE",FACE,{"derivedFrom":[makeQuery(id+"F3.opExtrude","CAP_FACE",FACE,{"disambiguationData":[OSD([sQuery(id+"F2.wireOp",EDGE,"E2.bottom"),sQuery(id+"F2.wireOp",EDGE,"E2.top"),sQuery(id+"F2.wireOp",EDGE,"E2.left"),sQuery(id+"F2.wireOp",EDGE,"E2.right"),sQuery(id+"F2.wireOp",EDGE,"E3.right")])],"isStart":false}),makeQuery(id+"F3.opExtrude","CAP_FACE",FACE,{"disambiguationData":[OSD([sQuery(id+"F2.wireOp",EDGE,"E4.bottom"),sQuery(id+"F2.wireOp",EDGE,"E4.top"),sQuery(id+"F2.wireOp",EDGE,"E4.left"),sQuery(id+"F2.wireOp",EDGE,"E4.right")])],"isStart":false}),makeQuery(id+"F5.opExtrude","CAP_FACE",FACE,{"disambiguationData":[OSD([sQuery(id+"F4.wireOp",EDGE,"E5.top"),sQuery(id+"F4.wireOp",EDGE,"E5.left"),sQuery(id+"F4.wireOp",EDGE,"E5.right"),sQuery(id+"F4.wireOp",EDGE,"E6.MirrorCS"),sQuery(id+"F4.wireOp",EDGE,"E7.MirrorCS"),sQuery(id+"F4.wireOp",EDGE,"E8.MirrorCS")])],"isStart":false})]});
            var sketch = newSketch(context, id + "F33", { "sketchPlane" : qUnion([Q0])});
            skLineSegment(sketch, "E58.bottom", {"start": v(-389.94, -40.13) * mm, "end": v(41.86, -40.13) * mm});
            skLineSegment(sketch, "E58.top", {"start": v(-389.94, 494.9) * mm, "end": v(41.86, 494.9) * mm});
            skLineSegment(sketch, "E58.left", {"start": v(-389.94, -40.13) * mm, "end": v(-389.94, 494.9) * mm});
            skLineSegment(sketch, "E58.right", {"start": v(41.86, -40.13) * mm, "end": v(41.86, 494.9) * mm});
            skSolve(sketch);
        }
        {
            var Q0;
            Q0=qSketchRegion(id+"F33",true);
            extrude(context, id + "F34", {"entities" : qUnion([Q0]), "depth" : 7.62 * mm, "offsetDistance" : 25.4 * mm});
        }
    });
